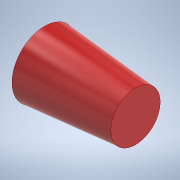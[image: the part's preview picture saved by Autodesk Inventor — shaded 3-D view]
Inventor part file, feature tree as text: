
AUTODESK INVENTOR PART (.ipt)
format: ipt  version: 2020 (Build 240168000, 168)  size: 104,960 bytes
history: native  units: mm
features: revolve x1, sketch x1
ambient origin geometry x8: Origin, YZ Plane, XZ Plane, XY Plane, X Axis, Y Axis, Z Axis, Center Point
bodies: Solid1 (feature_tree)
feature tree (2):
  revolve  "Revolution1"  [1 undecoded]
  sketch  "Sketch1"  dims[d0=4.75mm d1=17.5mm d2=6.25mm d3=90.0deg]
note: 1 required parameter value undecoded (feature->parameter linkage not recoverable at this tier; creation-order binding heuristic only, values carry confidence <= 0.55)
